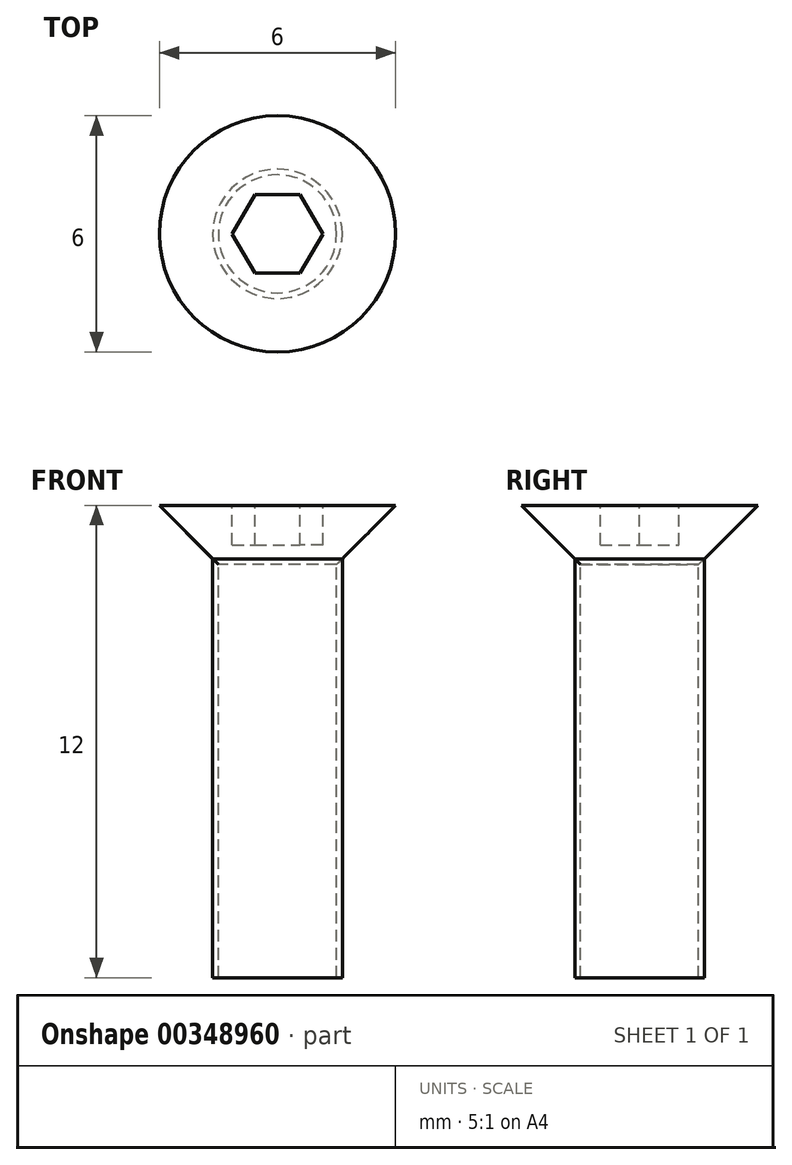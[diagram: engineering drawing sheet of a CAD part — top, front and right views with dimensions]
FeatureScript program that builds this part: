
annotation { "Feature Type Name" : "Feature", "Feature Type Description" : "" }
export const myFeature = defineFeature(function(context is Context, id is Id, definition is map)
    precondition{}
    {
        {
            var Q0;
            Q0=qCreatedBy(makeId("Top.planeOp"),FACE);
            var sketch = newSketch(context, id + "F0", { "sketchPlane" : qUnion([Q0])});
            skCircle(sketch, "E0", {"center": v(0, 0) * mm, "radius": 3 * mm});
            skCircle(sketch, "E1.cCircle", {"center": v(0, 0) * mm, "radius": 1 * mm, "construction": true});
            skLineSegment(sketch, "E1.0", {"start": v(-0.58, 1) * mm, "end": v(0.58, 1) * mm});
            skLineSegment(sketch, "E1.1", {"start": v(0.58, 1) * mm, "end": v(1.15, 0) * mm});
            skLineSegment(sketch, "E1.2", {"start": v(1.15, 0) * mm, "end": v(0.58, -1) * mm});
            skLineSegment(sketch, "E1.3", {"start": v(0.58, -1) * mm, "end": v(-0.58, -1) * mm});
            skLineSegment(sketch, "E1.4", {"start": v(-0.58, -1) * mm, "end": v(-1.15, 0) * mm});
            skLineSegment(sketch, "E1.5", {"start": v(-1.15, 0) * mm, "end": v(-0.58, 1) * mm});
            skPoint(sketch, "E1.0.midPoint", {"position": v(0, 1) * mm});
            skSolve(sketch);
        }
        {
            var Q0;
            Q0=qCreatedBy(makeId("Front.planeOp"),FACE);
            var sketch = newSketch(context, id + "F1", { "sketchPlane" : qUnion([Q0])});
            skLineSegment(sketch, "E2.0", {"start": v(-3, 0) * mm, "end": v(3, 0) * mm});
            skLineSegment(sketch, "E3", {"start": v(3, 0) * mm, "end": v(0, -3) * mm});
            skLineSegment(sketch, "E4", {"start": v(0, -3) * mm, "end": v(0, 0) * mm});
            skLineSegment(sketch, "E5", {"start": v(0, 0) * mm, "end": v(0, -12) * mm});
            skLineSegment(sketch, "E6", {"start": v(0, -12) * mm, "end": v(1.5, -12) * mm});
            skLineSegment(sketch, "E7", {"start": v(1.5, -12) * mm, "end": v(1.5, 0) * mm});
            skLineSegment(sketch, "E8", {"start": v(1.5, -12) * mm, "end": v(1.65, -12) * mm});
            skLineSegment(sketch, "E9", {"start": v(1.65, -12) * mm, "end": v(1.65, -1.35) * mm});
            skSolve(sketch);
        }
        {
            var Q0;
            {var subQ0=sQuery(id+"F1.wireOp",EDGE,"E3");var subQ1=sQuery(id+"F1.wireOp",EDGE,"E2.0");var subQ2=makeQuery(id+"F1.imprint","INTERSECT",VERTEX,{"derivedFrom":[subQ1,subQ0]});Q0=makeQuery(id+"F1.imprint","IMPRINT",FACE,{"disambiguationData":[TD([[makeQuery(id+"F1.imprint","IMPRINT",EDGE,{"disambiguationData":[TD([[subQ2,1.0]])],"derivedFrom":subQ1}),-1.0]])]});}
            var Q1;
            {var subQ0=sQuery(id+"F1.wireOp",EDGE,"E5");var subQ1=sQuery(id+"F1.wireOp",EDGE,"E2.0");var subQ2=makeQuery(id+"F1.imprint","INTERSECT",VERTEX,{"derivedFrom":[subQ1,subQ0]});Q1=makeQuery(id+"F1.imprint","IMPRINT",FACE,{"disambiguationData":[TD([[makeQuery(id+"F1.imprint","IMPRINT",EDGE,{"disambiguationData":[TD([[subQ2,-1.0]])],"derivedFrom":subQ1}),-1.0]])]});}
            var Q2;
            {var subQ5=sQuery(id+"F1.wireOp",EDGE,"E6");Q2=makeQuery(id+"F1.imprint","IMPRINT",FACE,{"disambiguationData":[TD([[makeQuery(id+"F1.imprint","IMPRINT",EDGE,{"derivedFrom":subQ5}),1.0]])]});}
            var Q3;
            Q3=sQuery(id+"F1.wireOp",EDGE,"E5");
            revolve(context, id + "F2", {"entities" : qUnion([Q0, Q1, Q2]), "axis" : qUnion([Q3]), "revolveType" : RevolveType.FULL});
        }
        {
            var Q0;
            Q0=makeQuery(id+"F0.imprint","IMPRINT",FACE,{"disambiguationData":[TD([[makeQuery(id+"F0.imprint","IMPRINT",EDGE,{"derivedFrom":sQuery(id+"F0.wireOp",EDGE,"E1.0")}),-1.0]])]});
            extrude(context, id + "F3", {"entities" : qUnion([Q0]), "operationType" : NewBodyOperationType.REMOVE, "oppositeDirection" : true, "depth" : 1 * mm});
        }
        {
            var Q0;
            {var subQ5=sQuery(id+"F1.wireOp",EDGE,"E6");Q0=makeQuery(id+"F1.imprint","IMPRINT",FACE,{"disambiguationData":[TD([[makeQuery(id+"F1.imprint","IMPRINT",EDGE,{"derivedFrom":subQ5}),1.0]])]});}
            var Q1;
            {var subQ0=sQuery(id+"F1.wireOp",EDGE,"E5");var subQ1=sQuery(id+"F1.wireOp",EDGE,"E2.0");var subQ2=makeQuery(id+"F1.imprint","INTERSECT",VERTEX,{"derivedFrom":[subQ1,subQ0]});Q1=makeQuery(id+"F1.imprint","IMPRINT",FACE,{"disambiguationData":[TD([[makeQuery(id+"F1.imprint","IMPRINT",EDGE,{"disambiguationData":[TD([[subQ2,-1.0]])],"derivedFrom":subQ1}),-1.0]])]});}
            var Q2;
            {var subQ0=sQuery(id+"F1.wireOp",EDGE,"E3");var subQ1=sQuery(id+"F1.wireOp",EDGE,"E2.0");var subQ2=makeQuery(id+"F1.imprint","INTERSECT",VERTEX,{"derivedFrom":[subQ1,subQ0]});Q2=makeQuery(id+"F1.imprint","IMPRINT",FACE,{"disambiguationData":[TD([[makeQuery(id+"F1.imprint","IMPRINT",EDGE,{"disambiguationData":[TD([[subQ2,1.0]])],"derivedFrom":subQ1}),-1.0]])]});}
            var Q3;
            {var subQ4=sQuery(id+"F1.wireOp",EDGE,"E8");Q3=makeQuery(id+"F1.imprint","IMPRINT",FACE,{"disambiguationData":[TD([[makeQuery(id+"F1.imprint","IMPRINT",EDGE,{"derivedFrom":subQ4}),1.0]])]});}
            var Q4;
            Q4=sQuery(id+"F1.wireOp",EDGE,"E5");
            revolve(context, id + "F4", {"entities" : qUnion([Q0, Q1, Q2, Q3]), "axis" : qUnion([Q4]), "revolveType" : RevolveType.FULL});
        }
    });
